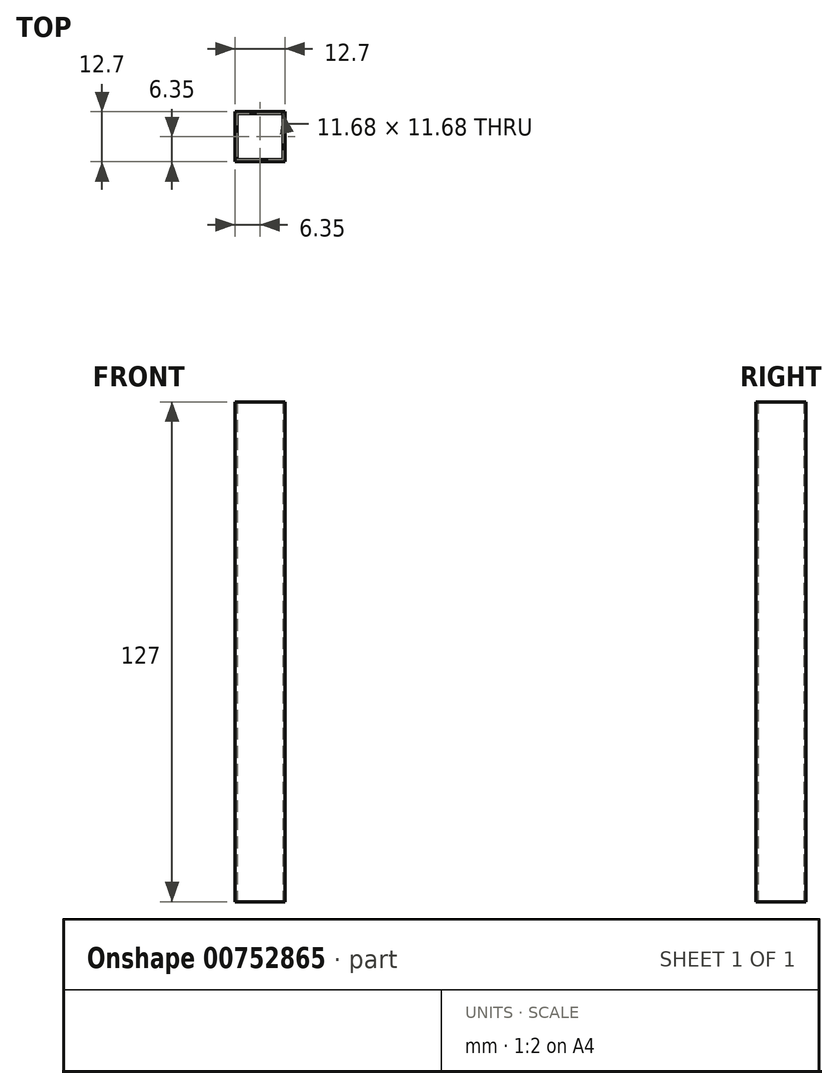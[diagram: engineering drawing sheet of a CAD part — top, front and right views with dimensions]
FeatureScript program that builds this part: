
annotation { "Feature Type Name" : "Feature", "Feature Type Description" : "" }
export const myFeature = defineFeature(function(context is Context, id is Id, definition is map)
    precondition{}
    {
        {
            var Q0;
            Q0=qCreatedBy(makeId("Top.planeOp"),FACE);
            var sketch = newSketch(context, id + "F0", { "sketchPlane" : qUnion([Q0])});
            skLineSegment(sketch, "E0.bottom", {"start": v(6.35, 6.35) * mm, "end": v(-6.35, 6.35) * mm});
            skLineSegment(sketch, "E0.top", {"start": v(6.35, -6.35) * mm, "end": v(-6.35, -6.35) * mm});
            skLineSegment(sketch, "E0.left", {"start": v(6.35, 6.35) * mm, "end": v(6.35, -6.35) * mm});
            skLineSegment(sketch, "E0.right", {"start": v(-6.35, 6.35) * mm, "end": v(-6.35, -6.35) * mm});
            skPoint(sketch, "E0.middle", {"position": v(0, 0) * mm});
            skLineSegment(sketch, "E1.bottom", {"start": v(5.84, -5.84) * mm, "end": v(-5.84, -5.84) * mm});
            skLineSegment(sketch, "E1.top", {"start": v(5.84, 5.84) * mm, "end": v(-5.84, 5.84) * mm});
            skLineSegment(sketch, "E1.left", {"start": v(5.84, -5.84) * mm, "end": v(5.84, 5.84) * mm});
            skLineSegment(sketch, "E1.right", {"start": v(-5.84, -5.84) * mm, "end": v(-5.84, 5.84) * mm});
            skSolve(sketch);
        }
        {
            var Q0;
            Q0=makeQuery(id+"F0.imprint","IMPRINT",FACE,{"disambiguationData":[TD([[makeQuery(id+"F0.imprint","IMPRINT",EDGE,{"derivedFrom":sQuery(id+"F0.wireOp",EDGE,"E0.bottom")}),1.0]])]});
            extrude(context, id + "F1", {"entities" : qUnion([Q0]), "depth" : 127 * mm, "offsetDistance" : 25.4 * mm});
        }
    });
